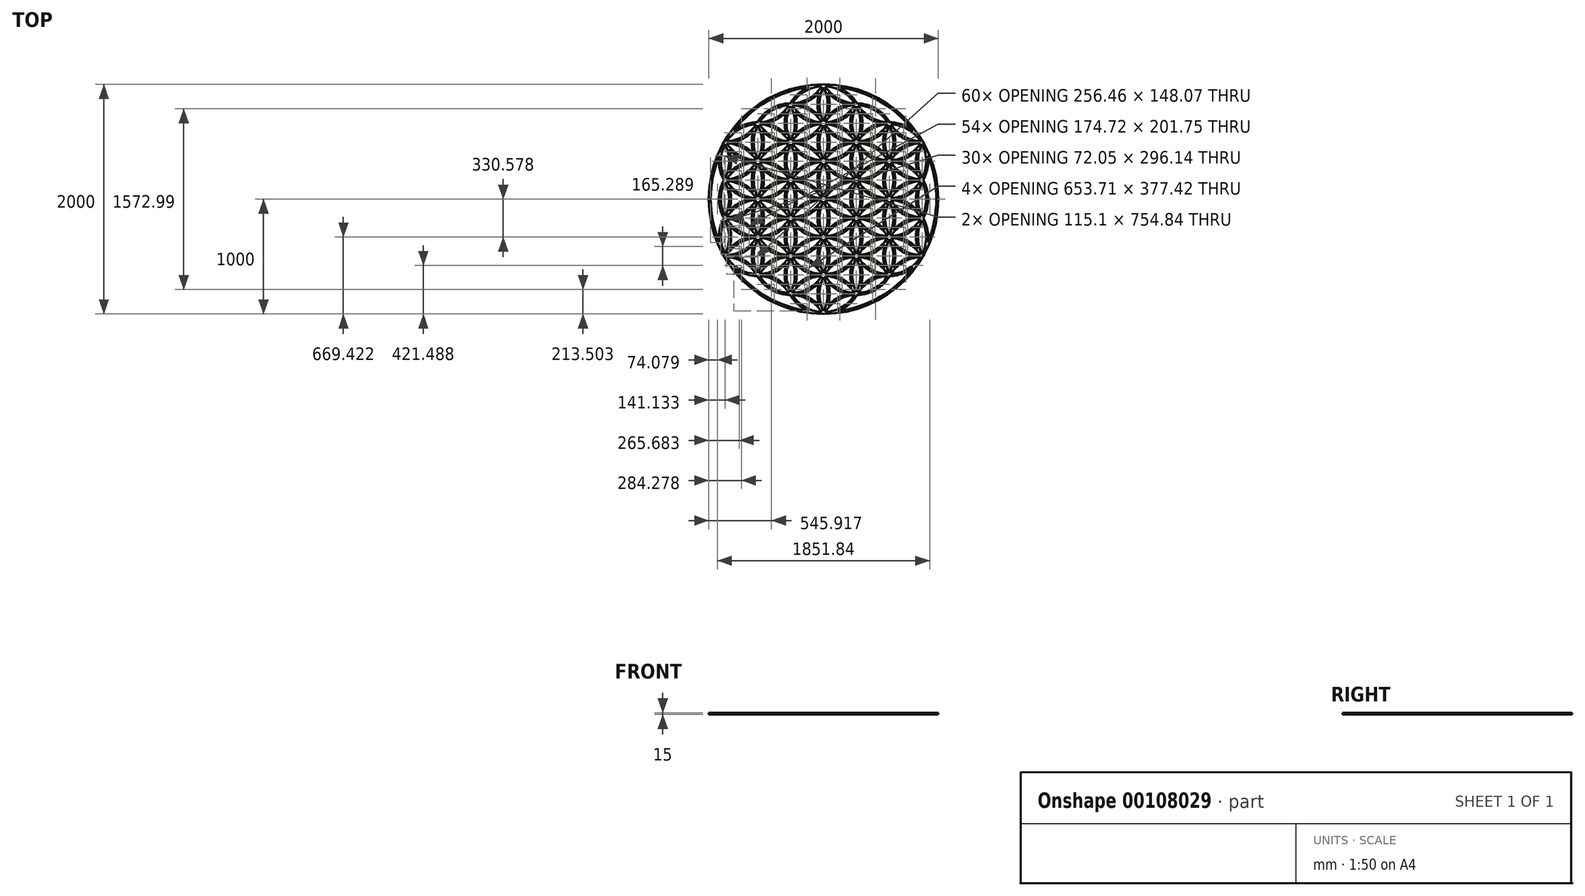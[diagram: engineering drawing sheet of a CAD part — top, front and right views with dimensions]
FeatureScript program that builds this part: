
annotation { "Feature Type Name" : "Feature", "Feature Type Description" : "" }
export const myFeature = defineFeature(function(context is Context, id is Id, definition is map)
    precondition{}
    {
        {
            var Q0;
            Q0=qCreatedBy(makeId("Top.planeOp"),FACE);
            var sketch = newSketch(context, id + "F0", { "sketchPlane" : qUnion([Q0])});
            skLineSegment(sketch, "E0", {"start": v(-500.18, -500) * mm, "end": v(-483.65, -500) * mm});
            skArc(sketch, "E1", {"start": v(228.44, -326.1) * mm, "mid": v(374.69, -283.26) * mm, "end": v(484.9, -178.03) * mm});
            skArc(sketch, "E2", {"start": v(484.9, -178.03) * mm, "mid": v(338.66, -220.87) * mm, "end": v(228.44, -326.1) * mm});
            skArc(sketch, "E3", {"start": v(287.91, -334.71) * mm, "mid": v(382.95, -297.58) * mm, "end": v(462.63, -233.84) * mm});
            skArc(sketch, "E4", {"start": v(499.82, -186.64) * mm, "mid": v(463.8, -334.71) * mm, "end": v(499.82, -482.78) * mm});
            skArc(sketch, "E5", {"start": v(462.63, -435.58) * mm, "mid": v(382.95, -371.84) * mm, "end": v(287.91, -334.71) * mm});
            skArc(sketch, "E6", {"start": v(462.63, -233.84) * mm, "mid": v(447.27, -334.71) * mm, "end": v(462.63, -435.58) * mm});
            skArc(sketch, "E7", {"start": v(484.9, -491.4) * mm, "mid": v(374.69, -386.16) * mm, "end": v(228.44, -343.32) * mm});
            skArc(sketch, "E8", {"start": v(249.56, -500) * mm, "mid": v(240.42, -423.8) * mm, "end": v(213.53, -351.93) * mm});
            skArc(sketch, "E9", {"start": v(266.09, -500) * mm, "mid": v(262.22, -448.98) * mm, "end": v(250.72, -399.13) * mm});
            skArc(sketch, "E10", {"start": v(228.44, -343.32) * mm, "mid": v(338.66, -448.55) * mm, "end": v(484.9, -491.4) * mm});
            skArc(sketch, "E11", {"start": v(250.72, -399.13) * mm, "mid": v(330.4, -462.87) * mm, "end": v(425.44, -500) * mm});
            skArc(sketch, "E12", {"start": v(213.89, -351.24) * mm, "mid": v(186.73, -423.43) * mm, "end": v(177.5, -500) * mm});
            skArc(sketch, "E13", {"start": v(228.44, 4.48) * mm, "mid": v(374.69, 47.31) * mm, "end": v(484.9, 152.55) * mm});
            skArc(sketch, "E14", {"start": v(484.9, 152.55) * mm, "mid": v(338.66, 109.71) * mm, "end": v(228.44, 4.48) * mm});
            skArc(sketch, "E15", {"start": v(287.91, -4.13) * mm, "mid": v(382.95, 33) * mm, "end": v(462.63, 96.74) * mm});
            skArc(sketch, "E16", {"start": v(499.82, 143.94) * mm, "mid": v(463.8, -4.13) * mm, "end": v(499.82, -152.2) * mm});
            skArc(sketch, "E17", {"start": v(462.63, -105) * mm, "mid": v(382.95, -41.26) * mm, "end": v(287.91, -4.13) * mm});
            skArc(sketch, "E18", {"start": v(462.63, 96.74) * mm, "mid": v(447.27, -4.13) * mm, "end": v(462.63, -105) * mm});
            skArc(sketch, "E19", {"start": v(484.9, -160.81) * mm, "mid": v(374.69, -55.58) * mm, "end": v(228.44, -12.74) * mm});
            skArc(sketch, "E20", {"start": v(213.53, -317.5) * mm, "mid": v(249.56, -169.42) * mm, "end": v(213.53, -21.35) * mm});
            skArc(sketch, "E21", {"start": v(250.72, -270.3) * mm, "mid": v(266.09, -169.42) * mm, "end": v(250.72, -68.55) * mm});
            skArc(sketch, "E22", {"start": v(228.44, -12.74) * mm, "mid": v(338.66, -117.98) * mm, "end": v(484.9, -160.81) * mm});
            skArc(sketch, "E23", {"start": v(425.44, -169.42) * mm, "mid": v(330.4, -206.55) * mm, "end": v(250.72, -270.3) * mm});
            skArc(sketch, "E24", {"start": v(250.72, -68.55) * mm, "mid": v(330.4, -132.29) * mm, "end": v(425.44, -169.42) * mm});
            skArc(sketch, "E25", {"start": v(213.89, -20.66) * mm, "mid": v(177.5, -169.03) * mm, "end": v(213.53, -317.5) * mm});
            skArc(sketch, "E26", {"start": v(228.44, 335.06) * mm, "mid": v(374.69, 377.9) * mm, "end": v(484.9, 483.13) * mm});
            skArc(sketch, "E27", {"start": v(484.9, 483.13) * mm, "mid": v(338.66, 440.29) * mm, "end": v(228.44, 335.06) * mm});
            skArc(sketch, "E28", {"start": v(287.91, 326.45) * mm, "mid": v(382.95, 363.58) * mm, "end": v(462.63, 427.32) * mm});
            skArc(sketch, "E29", {"start": v(499.82, 474.52) * mm, "mid": v(463.8, 326.45) * mm, "end": v(499.82, 178.38) * mm});
            skArc(sketch, "E30", {"start": v(462.63, 225.57) * mm, "mid": v(382.95, 289.31) * mm, "end": v(287.91, 326.45) * mm});
            skArc(sketch, "E31", {"start": v(462.63, 427.32) * mm, "mid": v(447.27, 326.45) * mm, "end": v(462.63, 225.57) * mm});
            skArc(sketch, "E32", {"start": v(484.9, 169.77) * mm, "mid": v(374.69, 275) * mm, "end": v(228.44, 317.84) * mm});
            skArc(sketch, "E33", {"start": v(213.53, 13.09) * mm, "mid": v(249.56, 161.16) * mm, "end": v(213.53, 309.23) * mm});
            skArc(sketch, "E34", {"start": v(250.72, 60.28) * mm, "mid": v(266.09, 161.16) * mm, "end": v(250.72, 262.03) * mm});
            skArc(sketch, "E35", {"start": v(228.44, 317.84) * mm, "mid": v(338.66, 212.6) * mm, "end": v(484.9, 169.77) * mm});
            skArc(sketch, "E36", {"start": v(425.44, 161.16) * mm, "mid": v(330.4, 124.03) * mm, "end": v(250.72, 60.28) * mm});
            skArc(sketch, "E37", {"start": v(250.72, 262.03) * mm, "mid": v(330.4, 198.29) * mm, "end": v(425.44, 161.16) * mm});
            skArc(sketch, "E38", {"start": v(213.89, 309.92) * mm, "mid": v(177.5, 161.55) * mm, "end": v(213.53, 13.09) * mm});
            skArc(sketch, "E39", {"start": v(500.18, 144.63) * mm, "mid": v(463.8, -3.74) * mm, "end": v(499.82, -152.2) * mm});
            skArc(sketch, "E40", {"start": v(-57.85, 169.77) * mm, "mid": v(88.4, 212.6) * mm, "end": v(198.62, 317.84) * mm});
            skArc(sketch, "E41", {"start": v(198.62, 317.84) * mm, "mid": v(52.37, 275) * mm, "end": v(-57.85, 169.77) * mm});
            skArc(sketch, "E42", {"start": v(1.62, 161.16) * mm, "mid": v(96.66, 198.29) * mm, "end": v(176.34, 262.03) * mm});
            skArc(sketch, "E43", {"start": v(213.53, 309.23) * mm, "mid": v(177.5, 161.16) * mm, "end": v(213.53, 13.09) * mm});
            skArc(sketch, "E44", {"start": v(176.34, 60.28) * mm, "mid": v(96.66, 124.03) * mm, "end": v(1.62, 161.16) * mm});
            skArc(sketch, "E45", {"start": v(176.34, 262.03) * mm, "mid": v(160.98, 161.16) * mm, "end": v(176.34, 60.28) * mm});
            skArc(sketch, "E46", {"start": v(198.62, 4.48) * mm, "mid": v(88.4, 109.71) * mm, "end": v(-57.85, 152.55) * mm});
            skArc(sketch, "E47", {"start": v(-72.76, -152.2) * mm, "mid": v(-36.73, -4.13) * mm, "end": v(-72.76, 143.94) * mm});
            skArc(sketch, "E48", {"start": v(-35.57, -105) * mm, "mid": v(-20.2, -4.13) * mm, "end": v(-35.57, 96.74) * mm});
            skArc(sketch, "E49", {"start": v(-57.85, 152.55) * mm, "mid": v(52.37, 47.31) * mm, "end": v(198.62, 4.48) * mm});
            skArc(sketch, "E50", {"start": v(139.15, -4.13) * mm, "mid": v(44.11, -41.26) * mm, "end": v(-35.57, -105) * mm});
            skArc(sketch, "E51", {"start": v(-35.57, 96.74) * mm, "mid": v(44.11, 33) * mm, "end": v(139.15, -4.13) * mm});
            skArc(sketch, "E52", {"start": v(198.62, -12.74) * mm, "mid": v(52.37, -55.58) * mm, "end": v(-57.85, -160.81) * mm});
            skArc(sketch, "E53", {"start": v(198.62, -326.1) * mm, "mid": v(88.4, -220.87) * mm, "end": v(-57.85, -178.03) * mm});
            skArc(sketch, "E54", {"start": v(176.34, -270.3) * mm, "mid": v(96.66, -206.55) * mm, "end": v(1.62, -169.42) * mm});
            skArc(sketch, "E55", {"start": v(-57.85, -160.81) * mm, "mid": v(88.4, -117.98) * mm, "end": v(198.62, -12.74) * mm});
            skArc(sketch, "E56", {"start": v(176.34, -68.55) * mm, "mid": v(160.98, -169.42) * mm, "end": v(176.34, -270.3) * mm});
            skArc(sketch, "E57", {"start": v(1.62, -169.42) * mm, "mid": v(96.66, -132.29) * mm, "end": v(176.34, -68.55) * mm});
            skArc(sketch, "E58", {"start": v(213.53, -21.35) * mm, "mid": v(177.5, -169.42) * mm, "end": v(213.53, -317.5) * mm});
            skArc(sketch, "E59", {"start": v(484.9, 169.77) * mm, "mid": v(374.35, 275.2) * mm, "end": v(227.67, 317.87) * mm});
            skArc(sketch, "E60", {"start": v(-57.85, -178.03) * mm, "mid": v(52.37, -283.26) * mm, "end": v(198.62, -326.1) * mm});
            skArc(sketch, "E61", {"start": v(-72.4, 144.63) * mm, "mid": v(-108.78, -3.74) * mm, "end": v(-72.76, -152.2) * mm});
            skArc(sketch, "E62", {"start": v(-72.76, -482.78) * mm, "mid": v(-36.73, -334.71) * mm, "end": v(-72.76, -186.64) * mm});
            skArc(sketch, "E63", {"start": v(-35.57, -435.58) * mm, "mid": v(-20.2, -334.71) * mm, "end": v(-35.57, -233.84) * mm});
            skArc(sketch, "E64", {"start": v(139.15, -334.71) * mm, "mid": v(44.11, -371.84) * mm, "end": v(-35.57, -435.58) * mm});
            skArc(sketch, "E65", {"start": v(-35.57, -233.84) * mm, "mid": v(44.11, -297.58) * mm, "end": v(139.15, -334.71) * mm});
            skArc(sketch, "E66", {"start": v(198.62, -343.32) * mm, "mid": v(52.37, -386.16) * mm, "end": v(-57.85, -491.4) * mm});
            skArc(sketch, "E67", {"start": v(-57.85, -491.4) * mm, "mid": v(88.4, -448.55) * mm, "end": v(198.62, -343.32) * mm});
            skArc(sketch, "E68", {"start": v(176.34, -399.13) * mm, "mid": v(164.84, -448.98) * mm, "end": v(160.98, -500) * mm});
            skArc(sketch, "E69", {"start": v(1.62, -500) * mm, "mid": v(96.66, -462.87) * mm, "end": v(176.34, -399.13) * mm});
            skArc(sketch, "E70", {"start": v(213.53, -351.93) * mm, "mid": v(186.64, -423.8) * mm, "end": v(177.5, -500) * mm});
            skArc(sketch, "E71", {"start": v(484.9, -160.81) * mm, "mid": v(374.35, -55.38) * mm, "end": v(227.67, -12.7) * mm});
            skArc(sketch, "E72", {"start": v(-72.4, -185.95) * mm, "mid": v(-108.78, -334.32) * mm, "end": v(-72.76, -482.78) * mm});
            skArc(sketch, "E73", {"start": v(484.9, -491.4) * mm, "mid": v(374.35, -385.96) * mm, "end": v(227.67, -343.29) * mm});
            skArc(sketch, "E74", {"start": v(-344.13, 4.48) * mm, "mid": v(-197.9, 47.31) * mm, "end": v(-87.67, 152.55) * mm});
            skArc(sketch, "E75", {"start": v(-87.67, 152.55) * mm, "mid": v(-233.91, 109.71) * mm, "end": v(-344.13, 4.48) * mm});
            skArc(sketch, "E76", {"start": v(-284.67, -4.13) * mm, "mid": v(-189.63, 33) * mm, "end": v(-109.95, 96.74) * mm});
            skArc(sketch, "E77", {"start": v(-72.76, 143.94) * mm, "mid": v(-108.78, -4.13) * mm, "end": v(-72.76, -152.2) * mm});
            skArc(sketch, "E78", {"start": v(-109.95, -105) * mm, "mid": v(-189.63, -41.26) * mm, "end": v(-284.67, -4.13) * mm});
            skArc(sketch, "E79", {"start": v(-109.95, 96.74) * mm, "mid": v(-125.31, -4.13) * mm, "end": v(-109.95, -105) * mm});
            skArc(sketch, "E80", {"start": v(-87.67, -160.81) * mm, "mid": v(-197.9, -55.58) * mm, "end": v(-344.13, -12.74) * mm});
            skArc(sketch, "E81", {"start": v(-359.05, -317.5) * mm, "mid": v(-323.02, -169.42) * mm, "end": v(-359.05, -21.35) * mm});
            skArc(sketch, "E82", {"start": v(-321.86, -270.3) * mm, "mid": v(-306.5, -169.42) * mm, "end": v(-321.86, -68.55) * mm});
            skArc(sketch, "E83", {"start": v(-344.13, -12.74) * mm, "mid": v(-233.91, -117.98) * mm, "end": v(-87.67, -160.81) * mm});
            skArc(sketch, "E84", {"start": v(-147.14, -169.42) * mm, "mid": v(-242.18, -206.55) * mm, "end": v(-321.86, -270.3) * mm});
            skArc(sketch, "E85", {"start": v(-321.86, -68.55) * mm, "mid": v(-242.18, -132.29) * mm, "end": v(-147.14, -169.42) * mm});
            skArc(sketch, "E86", {"start": v(-87.67, -178.03) * mm, "mid": v(-233.91, -220.87) * mm, "end": v(-344.13, -326.1) * mm});
            skArc(sketch, "E87", {"start": v(-87.67, -491.4) * mm, "mid": v(-197.9, -386.16) * mm, "end": v(-344.13, -343.32) * mm});
            skArc(sketch, "E88", {"start": v(-109.95, -435.58) * mm, "mid": v(-189.63, -371.84) * mm, "end": v(-284.67, -334.71) * mm});
            skArc(sketch, "E89", {"start": v(-344.13, -326.1) * mm, "mid": v(-197.9, -283.26) * mm, "end": v(-87.67, -178.03) * mm});
            skArc(sketch, "E90", {"start": v(-109.95, -233.84) * mm, "mid": v(-125.31, -334.71) * mm, "end": v(-109.95, -435.58) * mm});
            skArc(sketch, "E91", {"start": v(-284.67, -334.71) * mm, "mid": v(-189.63, -297.58) * mm, "end": v(-109.95, -233.84) * mm});
            skArc(sketch, "E92", {"start": v(-72.76, -186.64) * mm, "mid": v(-108.78, -334.71) * mm, "end": v(-72.76, -482.78) * mm});
            skArc(sketch, "E93", {"start": v(198.62, 4.48) * mm, "mid": v(88.06, 109.9) * mm, "end": v(-58.62, 152.58) * mm});
            skArc(sketch, "E94", {"start": v(-344.13, -343.32) * mm, "mid": v(-233.91, -448.55) * mm, "end": v(-87.67, -491.4) * mm});
            skArc(sketch, "E95", {"start": v(-358.69, -20.66) * mm, "mid": v(-395.07, -169.03) * mm, "end": v(-359.05, -317.5) * mm});
            skArc(sketch, "E96", {"start": v(-323.02, -500) * mm, "mid": v(-332.16, -423.8) * mm, "end": v(-359.05, -351.93) * mm});
            skArc(sketch, "E97", {"start": v(-306.5, -500) * mm, "mid": v(-310.36, -448.98) * mm, "end": v(-321.86, -399.13) * mm});
            skArc(sketch, "E98", {"start": v(-321.86, -399.13) * mm, "mid": v(-242.18, -462.87) * mm, "end": v(-147.14, -500) * mm});
            skArc(sketch, "E99", {"start": v(198.62, -326.1) * mm, "mid": v(88.06, -220.67) * mm, "end": v(-58.62, -178) * mm});
            skArc(sketch, "E100", {"start": v(499.82, 500) * mm, "mid": v(-207.29, 207.1) * mm, "end": v(-500.18, -500) * mm});
            skArc(sketch, "E101", {"start": v(372.6, 475.2) * mm, "mid": v(193.51, 306.03) * mm, "end": v(176.34, 60.28) * mm});
            skArc(sketch, "E102", {"start": v(372.6, 475.2) * mm, "mid": v(8.09, 351.71) * mm, "end": v(-281.12, 97.79) * mm});
            skArc(sketch, "E103", {"start": v(-408.35, -122.58) * mm, "mid": v(-464.64, -307.57) * mm, "end": v(-483.65, -500) * mm});
            skArc(sketch, "E104", {"start": v(-359.05, -351.93) * mm, "mid": v(-385.94, -423.8) * mm, "end": v(-395.07, -500) * mm});
            skArc(sketch, "E105", {"start": v(-408.35, -122.58) * mm, "mid": v(-405.8, -231.9) * mm, "end": v(-368.55, -334.71) * mm});
            skArc(sketch, "E106", {"start": v(-368.55, -334.71) * mm, "mid": v(-400.66, -414.6) * mm, "end": v(-411.6, -500) * mm});
            skArc(sketch, "E107", {"start": v(-77.51, 169.39) * mm, "mid": v(-185.17, 150.23) * mm, "end": v(-281.12, 97.79) * mm});
            skArc(sketch, "E108", {"start": v(208.78, 334.68) * mm, "mid": v(44.11, 289.31) * mm, "end": v(-77.51, 169.39) * mm});
            skLineSegment(sketch, "E109", {"start": v(499.82, 500) * mm, "end": v(499.82, 474.52) * mm});
            skLineSegment(sketch, "E110", {"start": v(499.82, 178.38) * mm, "end": v(499.82, 143.94) * mm});
            skLineSegment(sketch, "E111", {"start": v(499.82, -152.2) * mm, "end": v(499.82, -186.64) * mm});
            skLineSegment(sketch, "E112", {"start": v(499.82, -482.78) * mm, "end": v(499.82, -500) * mm});
            skLineSegment(sketch, "E113", {"start": v(425.44, -500) * mm, "end": v(499.82, -500) * mm});
            skLineSegment(sketch, "E114", {"start": v(249.56, -500) * mm, "end": v(266.09, -500) * mm});
            skLineSegment(sketch, "E115", {"start": v(160.98, -500) * mm, "end": v(177.5, -500) * mm});
            skLineSegment(sketch, "E116", {"start": v(-147.14, -500) * mm, "end": v(1.62, -500) * mm});
            skLineSegment(sketch, "E117", {"start": v(-411.6, -500) * mm, "end": v(-395.07, -500) * mm});
            skLineSegment(sketch, "E118", {"start": v(-323.02, -500) * mm, "end": v(-306.5, -500) * mm});
            skSolve(sketch);
        }
        {
            var Q0;
            Q0 = qSketchRegion(id + "F0", true);
            extrude(context, id + "F1", {"entities" : qUnion([Q0]), "depth" : 15 * mm});
        }
        {
            var Q0;
            Q0=makeQuery(id+"F1.opExtrude","SWEPT_BODY",BODY,{"disambiguationData":[OSD([sQuery(id+"F0.wireOp",EDGE,"E0"),sQuery(id+"F0.wireOp",EDGE,"E26"),sQuery(id+"F0.wireOp",EDGE,"E27"),sQuery(id+"F0.wireOp",EDGE,"E28"),sQuery(id+"F0.wireOp",EDGE,"E29"),sQuery(id+"F0.wireOp",EDGE,"E31"),sQuery(id+"F0.wireOp",EDGE,"E40"),sQuery(id+"F0.wireOp",EDGE,"E41"),sQuery(id+"F0.wireOp",EDGE,"E42"),sQuery(id+"F0.wireOp",EDGE,"E16"),sQuery(id+"F0.wireOp",EDGE,"E35"),sQuery(id+"F0.wireOp",EDGE,"E37"),sQuery(id+"F0.wireOp",EDGE,"E13"),sQuery(id+"F0.wireOp",EDGE,"E33"),sQuery(id+"F0.wireOp",EDGE,"E59"),sQuery(id+"F0.wireOp",EDGE,"E43"),sQuery(id+"F0.wireOp",EDGE,"E15"),sQuery(id+"F0.wireOp",EDGE,"E14"),sQuery(id+"F0.wireOp",EDGE,"E34"),sQuery(id+"F0.wireOp",EDGE,"E4"),sQuery(id+"F0.wireOp",EDGE,"E22"),sQuery(id+"F0.wireOp",EDGE,"E1"),sQuery(id+"F0.wireOp",EDGE,"E71"),sQuery(id+"F0.wireOp",EDGE,"E2"),sQuery(id+"F0.wireOp",EDGE,"E10"),sQuery(id+"F0.wireOp",EDGE,"E73"),sQuery(id+"F0.wireOp",EDGE,"E74"),sQuery(id+"F0.wireOp",EDGE,"E75"),sQuery(id+"F0.wireOp",EDGE,"E76"),sQuery(id+"F0.wireOp",EDGE,"E81"),sQuery(id+"F0.wireOp",EDGE,"E82"),sQuery(id+"F0.wireOp",EDGE,"E80"),sQuery(id+"F0.wireOp",EDGE,"E58"),sQuery(id+"F0.wireOp",EDGE,"E49"),sQuery(id+"F0.wireOp",EDGE,"E51"),sQuery(id+"F0.wireOp",EDGE,"E55"),sQuery(id+"F0.wireOp",EDGE,"E47"),sQuery(id+"F0.wireOp",EDGE,"E83"),sQuery(id+"F0.wireOp",EDGE,"E93"),sQuery(id+"F0.wireOp",EDGE,"E77"),sQuery(id+"F0.wireOp",EDGE,"E57"),sQuery(id+"F0.wireOp",EDGE,"E85"),sQuery(id+"F0.wireOp",EDGE,"E52"),sQuery(id+"F0.wireOp",EDGE,"E20"),sQuery(id+"F0.wireOp",EDGE,"E48"),sQuery(id+"F0.wireOp",EDGE,"E95"),sQuery(id+"F0.wireOp",EDGE,"E78"),sQuery(id+"F0.wireOp",EDGE,"E89"),sQuery(id+"F0.wireOp",EDGE,"E86"),sQuery(id+"F0.wireOp",EDGE,"E91"),sQuery(id+"F0.wireOp",EDGE,"E96"),sQuery(id+"F0.wireOp",EDGE,"E97"),sQuery(id+"F0.wireOp",EDGE,"E87"),sQuery(id+"F0.wireOp",EDGE,"E70"),sQuery(id+"F0.wireOp",EDGE,"E60"),sQuery(id+"F0.wireOp",EDGE,"E67"),sQuery(id+"F0.wireOp",EDGE,"E62"),sQuery(id+"F0.wireOp",EDGE,"E94"),sQuery(id+"F0.wireOp",EDGE,"E99"),sQuery(id+"F0.wireOp",EDGE,"E92"),sQuery(id+"F0.wireOp",EDGE,"E66"),sQuery(id+"F0.wireOp",EDGE,"E8"),sQuery(id+"F0.wireOp",EDGE,"E63"),sQuery(id+"F0.wireOp",EDGE,"E88"),sQuery(id+"F0.wireOp",EDGE,"E30"),sQuery(id+"F0.wireOp",EDGE,"E18"),sQuery(id+"F0.wireOp",EDGE,"E90"),sQuery(id+"F0.wireOp",EDGE,"E36"),sQuery(id+"F0.wireOp",EDGE,"E24"),sQuery(id+"F0.wireOp",EDGE,"E50"),sQuery(id+"F0.wireOp",EDGE,"E17"),sQuery(id+"F0.wireOp",EDGE,"E23"),sQuery(id+"F0.wireOp",EDGE,"E54"),sQuery(id+"F0.wireOp",EDGE,"E56"),sQuery(id+"F0.wireOp",EDGE,"E64"),sQuery(id+"F0.wireOp",EDGE,"E65"),sQuery(id+"F0.wireOp",EDGE,"E69"),sQuery(id+"F0.wireOp",EDGE,"E3"),sQuery(id+"F0.wireOp",EDGE,"E21"),sQuery(id+"F0.wireOp",EDGE,"E5"),sQuery(id+"F0.wireOp",EDGE,"E6"),sQuery(id+"F0.wireOp",EDGE,"E11"),sQuery(id+"F0.wireOp",EDGE,"E9"),sQuery(id+"F0.wireOp",EDGE,"E68"),sQuery(id+"F0.wireOp",EDGE,"E100"),sQuery(id+"F0.wireOp",EDGE,"E101"),sQuery(id+"F0.wireOp",EDGE,"E102"),sQuery(id+"F0.wireOp",EDGE,"E103"),sQuery(id+"F0.wireOp",EDGE,"E84"),sQuery(id+"F0.wireOp",EDGE,"E104"),sQuery(id+"F0.wireOp",EDGE,"E105"),sQuery(id+"F0.wireOp",EDGE,"E98"),sQuery(id+"F0.wireOp",EDGE,"E106"),sQuery(id+"F0.wireOp",EDGE,"E107"),sQuery(id+"F0.wireOp",EDGE,"E44"),sQuery(id+"F0.wireOp",EDGE,"E79"),sQuery(id+"F0.wireOp",EDGE,"E108"),sQuery(id+"F0.wireOp",EDGE,"E109"),sQuery(id+"F0.wireOp",EDGE,"E110"),sQuery(id+"F0.wireOp",EDGE,"E111"),sQuery(id+"F0.wireOp",EDGE,"E112"),sQuery(id+"F0.wireOp",EDGE,"E113"),sQuery(id+"F0.wireOp",EDGE,"E114"),sQuery(id+"F0.wireOp",EDGE,"E115"),sQuery(id+"F0.wireOp",EDGE,"E116"),sQuery(id+"F0.wireOp",EDGE,"E117"),sQuery(id+"F0.wireOp",EDGE,"E118")])]});
            var Q1;
            Q1=makeQuery(id+"F1.opExtrude","SWEPT_FACE",FACE,{"disambiguationData":[OSD([sQuery(id+"F0.wireOp",EDGE,"E109")])]});
            mirror(context, id + "F2", {"operationType" : NewBodyOperationType.ADD, "entities" : qUnion([Q0]), "mirrorPlane" : qUnion([Q1])});
        }
        {
            var Q0;
            Q0=makeQuery(id+"F1.opExtrude","SWEPT_BODY",BODY,{"disambiguationData":[OSD([sQuery(id+"F0.wireOp",EDGE,"E0"),sQuery(id+"F0.wireOp",EDGE,"E26"),sQuery(id+"F0.wireOp",EDGE,"E27"),sQuery(id+"F0.wireOp",EDGE,"E28"),sQuery(id+"F0.wireOp",EDGE,"E29"),sQuery(id+"F0.wireOp",EDGE,"E31"),sQuery(id+"F0.wireOp",EDGE,"E40"),sQuery(id+"F0.wireOp",EDGE,"E41"),sQuery(id+"F0.wireOp",EDGE,"E42"),sQuery(id+"F0.wireOp",EDGE,"E16"),sQuery(id+"F0.wireOp",EDGE,"E35"),sQuery(id+"F0.wireOp",EDGE,"E37"),sQuery(id+"F0.wireOp",EDGE,"E13"),sQuery(id+"F0.wireOp",EDGE,"E33"),sQuery(id+"F0.wireOp",EDGE,"E59"),sQuery(id+"F0.wireOp",EDGE,"E43"),sQuery(id+"F0.wireOp",EDGE,"E15"),sQuery(id+"F0.wireOp",EDGE,"E14"),sQuery(id+"F0.wireOp",EDGE,"E34"),sQuery(id+"F0.wireOp",EDGE,"E4"),sQuery(id+"F0.wireOp",EDGE,"E22"),sQuery(id+"F0.wireOp",EDGE,"E1"),sQuery(id+"F0.wireOp",EDGE,"E71"),sQuery(id+"F0.wireOp",EDGE,"E2"),sQuery(id+"F0.wireOp",EDGE,"E10"),sQuery(id+"F0.wireOp",EDGE,"E73"),sQuery(id+"F0.wireOp",EDGE,"E74"),sQuery(id+"F0.wireOp",EDGE,"E75"),sQuery(id+"F0.wireOp",EDGE,"E76"),sQuery(id+"F0.wireOp",EDGE,"E81"),sQuery(id+"F0.wireOp",EDGE,"E82"),sQuery(id+"F0.wireOp",EDGE,"E80"),sQuery(id+"F0.wireOp",EDGE,"E58"),sQuery(id+"F0.wireOp",EDGE,"E49"),sQuery(id+"F0.wireOp",EDGE,"E51"),sQuery(id+"F0.wireOp",EDGE,"E55"),sQuery(id+"F0.wireOp",EDGE,"E47"),sQuery(id+"F0.wireOp",EDGE,"E83"),sQuery(id+"F0.wireOp",EDGE,"E93"),sQuery(id+"F0.wireOp",EDGE,"E77"),sQuery(id+"F0.wireOp",EDGE,"E57"),sQuery(id+"F0.wireOp",EDGE,"E85"),sQuery(id+"F0.wireOp",EDGE,"E52"),sQuery(id+"F0.wireOp",EDGE,"E20"),sQuery(id+"F0.wireOp",EDGE,"E48"),sQuery(id+"F0.wireOp",EDGE,"E95"),sQuery(id+"F0.wireOp",EDGE,"E78"),sQuery(id+"F0.wireOp",EDGE,"E89"),sQuery(id+"F0.wireOp",EDGE,"E86"),sQuery(id+"F0.wireOp",EDGE,"E91"),sQuery(id+"F0.wireOp",EDGE,"E96"),sQuery(id+"F0.wireOp",EDGE,"E97"),sQuery(id+"F0.wireOp",EDGE,"E87"),sQuery(id+"F0.wireOp",EDGE,"E70"),sQuery(id+"F0.wireOp",EDGE,"E60"),sQuery(id+"F0.wireOp",EDGE,"E67"),sQuery(id+"F0.wireOp",EDGE,"E62"),sQuery(id+"F0.wireOp",EDGE,"E94"),sQuery(id+"F0.wireOp",EDGE,"E99"),sQuery(id+"F0.wireOp",EDGE,"E92"),sQuery(id+"F0.wireOp",EDGE,"E66"),sQuery(id+"F0.wireOp",EDGE,"E8"),sQuery(id+"F0.wireOp",EDGE,"E63"),sQuery(id+"F0.wireOp",EDGE,"E88"),sQuery(id+"F0.wireOp",EDGE,"E30"),sQuery(id+"F0.wireOp",EDGE,"E18"),sQuery(id+"F0.wireOp",EDGE,"E90"),sQuery(id+"F0.wireOp",EDGE,"E36"),sQuery(id+"F0.wireOp",EDGE,"E24"),sQuery(id+"F0.wireOp",EDGE,"E50"),sQuery(id+"F0.wireOp",EDGE,"E17"),sQuery(id+"F0.wireOp",EDGE,"E23"),sQuery(id+"F0.wireOp",EDGE,"E54"),sQuery(id+"F0.wireOp",EDGE,"E56"),sQuery(id+"F0.wireOp",EDGE,"E64"),sQuery(id+"F0.wireOp",EDGE,"E65"),sQuery(id+"F0.wireOp",EDGE,"E69"),sQuery(id+"F0.wireOp",EDGE,"E3"),sQuery(id+"F0.wireOp",EDGE,"E21"),sQuery(id+"F0.wireOp",EDGE,"E5"),sQuery(id+"F0.wireOp",EDGE,"E6"),sQuery(id+"F0.wireOp",EDGE,"E11"),sQuery(id+"F0.wireOp",EDGE,"E9"),sQuery(id+"F0.wireOp",EDGE,"E68"),sQuery(id+"F0.wireOp",EDGE,"E100"),sQuery(id+"F0.wireOp",EDGE,"E101"),sQuery(id+"F0.wireOp",EDGE,"E102"),sQuery(id+"F0.wireOp",EDGE,"E103"),sQuery(id+"F0.wireOp",EDGE,"E84"),sQuery(id+"F0.wireOp",EDGE,"E104"),sQuery(id+"F0.wireOp",EDGE,"E105"),sQuery(id+"F0.wireOp",EDGE,"E98"),sQuery(id+"F0.wireOp",EDGE,"E106"),sQuery(id+"F0.wireOp",EDGE,"E107"),sQuery(id+"F0.wireOp",EDGE,"E44"),sQuery(id+"F0.wireOp",EDGE,"E79"),sQuery(id+"F0.wireOp",EDGE,"E108"),sQuery(id+"F0.wireOp",EDGE,"E109"),sQuery(id+"F0.wireOp",EDGE,"E110"),sQuery(id+"F0.wireOp",EDGE,"E111"),sQuery(id+"F0.wireOp",EDGE,"E112"),sQuery(id+"F0.wireOp",EDGE,"E113"),sQuery(id+"F0.wireOp",EDGE,"E114"),sQuery(id+"F0.wireOp",EDGE,"E115"),sQuery(id+"F0.wireOp",EDGE,"E116"),sQuery(id+"F0.wireOp",EDGE,"E117"),sQuery(id+"F0.wireOp",EDGE,"E118")])]});
            var Q1;
            {var subQ0=makeQuery(id+"F1.opExtrude","SWEPT_FACE",FACE,{"disambiguationData":[OSD([sQuery(id+"F0.wireOp",EDGE,"E113")])]});Q1=makeQuery(id+"F2.boolean.opBoolean","MERGE",FACE,{"derivedFrom":[subQ0,makeQuery(id+"F2.opPattern","COPY",FACE,{"derivedFrom":subQ0,"instanceName":"1"})]});}
            mirror(context, id + "F3", {"operationType" : NewBodyOperationType.ADD, "entities" : qUnion([Q0]), "mirrorPlane" : qUnion([Q1])});
        }
    });
